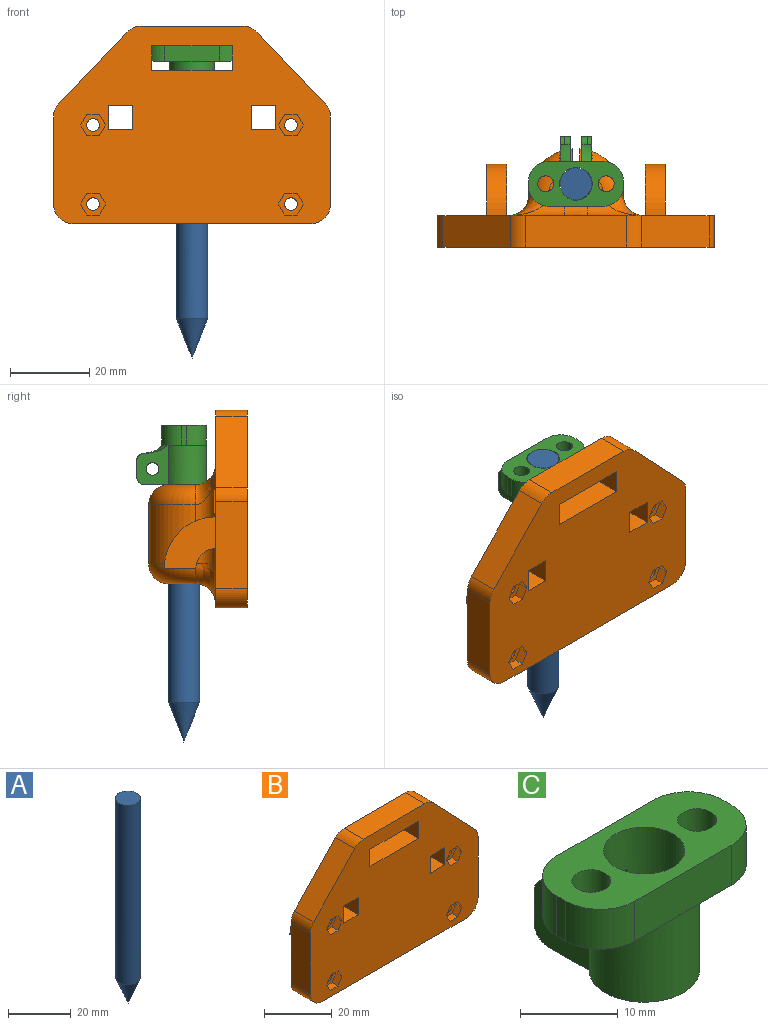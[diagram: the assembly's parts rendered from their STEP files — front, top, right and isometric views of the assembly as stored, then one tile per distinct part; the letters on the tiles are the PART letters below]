
ASSEMBLY  parts=3 mates=3
PART A: 3 faces, bbox 8x8x80 mm
  f0: cylinder r=4mm len=70mm, axis (0,0,1), area 1759.3mm2, adj f1,f2
  f1: plane 8x8mm, normal (0,0,1), area 50.3mm2, adj f0
  f2: cone r=0mm half-angle=21.8deg, axis (0,0,1), area 135.3mm2, adj f0
PART B: 189 faces, bbox 70.4x26.2x50.4 mm
  f0: plane 70x50mm, normal (0,1,0), area 1597.9mm2, adj f8,f9,f11,f12,f13,f14,f15,f16
  f1: plane 6.62x4.98mm, normal (0,0,1), area 13.5mm2, adj f6,f80,f89
  f2: plane 6.62x4.98mm, normal (0,0,-1), area 13.5mm2, adj f6,f85,f88
  f3: cylinder r=12mm len=15mm, axis (0,0,-1), area 266.9mm2, adj f69,f77,f78,f89,f90
  f4: plane 6.62x4.98mm, normal (0,0,1), area 13.5mm2, adj f6,f84,f92
  f5: plane 6.62x4.98mm, normal (0,0,-1), area 13.5mm2, adj f6,f77,f81
  f6: cylinder r=4.15mm len=25mm, axis (0,0,1), area 601.4mm2, adj f1,f2,f4,f5,f69,f70,f77,f82
  f7: plane 8x5mm, normal (0,0,-1), area 40mm2, adj f8,f9,f61,f64
  f8: cylinder r=5mm len=5mm, axis (-1,0,0), area 39.3mm2, adj f0,f7,f61,f64
  f9: cylinder r=13mm len=13mm, axis (-1,0,0), area 102.1mm2, adj f0,f7,f61,f64
  f10: plane 70x50mm, normal (0,-1,0), area 2758.9mm2, adj f15,f16,f17,f18,f19,f20,f21,f22
  f11: cylinder r=1.6mm len=5.5mm, axis (0,-1,0), area 55.3mm2, adj f0,f51
  f12: cylinder r=1.6mm len=5.5mm, axis (0,-1,0), area 55.3mm2, adj f0,f44
  f13: cylinder r=1.6mm len=5.5mm, axis (0,-1,0), area 55.3mm2, adj f0,f37
  f14: cylinder r=1.6mm len=5.5mm, axis (0,-1,0), area 55.3mm2, adj f0,f30
  f15: plane 22x8mm, normal (-1,0,0), area 176mm2, adj f0,f10,f74,f75
  f16: plane 60x8mm, normal (0,0,-1), area 480mm2, adj f0,f10,f75,f76
  f17: plane 22x8mm, normal (1,0,0), area 176mm2, adj f0,f10,f71,f76
  f18: plane 8.42x6.2mm, normal (0,0,-1), area 49.9mm2, adj f0,f10,f19,f21,f78
  f19: plane 8x6.2mm, normal (1,0,0), area 49.6mm2, adj f0,f10,f18,f20
  f20: plane 8.42x6.2mm, normal (0,0,1), area 49.9mm2, adj f0,f10,f19,f21,f78
  f21: plane 8.42x6.2mm, normal (-1,0,0), area 52.2mm2, adj f10,f18,f20,f78
  f22: plane 8x6.2mm, normal (-1,0,0), area 49.6mm2, adj f0,f10,f23,f25
  f23: plane 8.42x6.2mm, normal (0,0,-1), area 49.9mm2, adj f0,f10,f22,f24,f86
  f24: plane 8.42x6.2mm, normal (1,0,0), area 52.2mm2, adj f10,f23,f25,f86
  f25: plane 8.42x6.2mm, normal (0,0,1), area 49.9mm2, adj f0,f10,f22,f24,f86
  f26: plane 20.4x8mm, normal (0,0,-1), area 163.2mm2, adj f0,f10,f27,f29
  f27: plane 8x6.2mm, normal (1,0,0), area 49.6mm2, adj f0,f10,f26,f28
  f28: plane 20.4x8mm, normal (0,0,1), area 163.2mm2, adj f0,f10,f27,f29
  f29: plane 8x6.2mm, normal (-1,0,0), area 49.6mm2, adj f0,f10,f26,f28
  f30: plane 6.3x5.46mm, normal (0,-1,0), area 17.7mm2, adj f14,f31,f32,f33,f34,f35,f36
  f31: plane 3.15x2.5mm, normal (0,0,1), area 7.9mm2, adj f10,f30,f32,f36
  f32: plane 2.73x2.5mm, normal (-0.87,0,0.5), area 7.9mm2, adj f10,f30,f31,f33
  f33: plane 2.73x2.5mm, normal (-0.87,0,-0.5), area 7.9mm2, adj f10,f30,f32,f34
  f34: plane 3.15x2.5mm, normal (0,0,-1), area 7.9mm2, adj f10,f30,f33,f35
  f35: plane 2.73x2.5mm, normal (0.87,0,-0.5), area 7.9mm2, adj f10,f30,f34,f36
  f36: plane 2.73x2.5mm, normal (0.87,0,0.5), area 7.9mm2, adj f10,f30,f31,f35
  f37: plane 6.3x5.46mm, normal (0,-1,0), area 17.7mm2, adj f13,f38,f39,f40,f41,f42,f43
  f38: plane 3.15x2.5mm, normal (0,0,1), area 7.9mm2, adj f10,f37,f39,f43
  f39: plane 2.73x2.5mm, normal (-0.87,0,0.5), area 7.9mm2, adj f10,f37,f38,f40
  f40: plane 2.73x2.5mm, normal (-0.87,0,-0.5), area 7.9mm2, adj f10,f37,f39,f41
  f41: plane 3.15x2.5mm, normal (0,0,-1), area 7.9mm2, adj f10,f37,f40,f42
  f42: plane 2.73x2.5mm, normal (0.87,0,-0.5), area 7.9mm2, adj f10,f37,f41,f43
  f43: plane 2.73x2.5mm, normal (0.87,0,0.5), area 7.9mm2, adj f10,f37,f38,f42
  f44: plane 6.4x5.54mm, normal (0,-1,0), area 18.6mm2, adj f12,f45,f46,f47,f48,f49,f50
  f45: plane 3.2x2.5mm, normal (0,0,1), area 8mm2, adj f10,f44,f46,f50
  f46: plane 2.77x2.5mm, normal (-0.87,0,0.5), area 8mm2, adj f10,f44,f45,f47
  f47: plane 2.77x2.5mm, normal (-0.87,0,-0.5), area 8mm2, adj f10,f44,f46,f48
  f48: plane 3.2x2.5mm, normal (0,0,-1), area 8mm2, adj f10,f44,f47,f49
  f49: plane 2.77x2.5mm, normal (0.87,0,-0.5), area 8mm2, adj f10,f44,f48,f50
  f50: plane 2.77x2.5mm, normal (0.87,0,0.5), area 8mm2, adj f10,f44,f45,f49
  f51: plane 6.4x5.54mm, normal (0,-1,0), area 18.6mm2, adj f11,f52,f53,f54,f55,f56,f57
  f52: plane 2.77x2.5mm, normal (-0.87,0,0.5), area 8mm2, adj f10,f51,f53,f57
  f53: plane 2.77x2.5mm, normal (-0.87,0,-0.5), area 8mm2, adj f10,f51,f52,f54
  f54: plane 3.2x2.5mm, normal (0,0,-1), area 8mm2, adj f10,f51,f53,f55
  f55: plane 2.77x2.5mm, normal (0.87,0,-0.5), area 8mm2, adj f10,f51,f54,f56
  f56: plane 2.77x2.5mm, normal (0.87,0,0.5), area 8mm2, adj f10,f51,f55,f57
  f57: plane 3.2x2.5mm, normal (0,0,1), area 8mm2, adj f10,f51,f52,f56
  f58: cylinder r=5mm len=5mm, axis (-1,0,0), area 39.3mm2, adj f0,f59,f62,f63
  f59: plane 8x5mm, normal (0,0,-1), area 40mm2, adj f58,f60,f62,f63
  f60: cylinder r=13mm len=13mm, axis (-1,0,0), area 102.1mm2, adj f0,f59,f62,f63
  f61: plane 13x13mm, normal (1,0,0), area 113.1mm2, adj f0,f7,f8,f9
  f62: plane 13x13mm, normal (-1,0,0), area 113.1mm2, adj f0,f58,f59,f60
  f63: plane 13x13mm, normal (1,0,0), area 113.1mm2, adj f0,f58,f59,f60
  f64: plane 13x13mm, normal (-1,0,0), area 113.1mm2, adj f0,f7,f8,f9
  f65: cylinder r=12mm len=15mm, axis (0,0,-1), area 266.9mm2, adj f70,f86,f88,f92,f93
  f66: plane 18x17.15mm, normal (0.72,0,0.69), area 198.9mm2, adj f0,f10,f71,f72
  f67: plane 25.7x8mm, normal (0,0,1), area 205.6mm2, adj f0,f10,f72,f73
  f68: plane 18x17.15mm, normal (-0.72,0,0.69), area 198.9mm2, adj f0,f10,f73,f74
  f69: plane 25.36x5.21mm, normal (1,0,0), area 110.5mm2, adj f3,f6,f77,f89
  f70: plane 25.36x5.21mm, normal (-1,0,0), area 110.5mm2, adj f6,f65,f88,f92
  f71: cylinder r=5mm len=8mm, axis (0,-1,0), area 30.4mm2, adj f0,f10,f17,f66
  f72: cylinder r=5mm len=8mm, axis (0,1,0), area 32.4mm2, adj f0,f10,f66,f67
  f73: cylinder r=5mm len=8mm, axis (0,-1,0), area 32.4mm2, adj f0,f10,f67,f68
  f74: cylinder r=5mm len=8mm, axis (0,-1,0), area 30.4mm2, adj f0,f10,f15,f68
  f75: cylinder r=5mm len=8mm, axis (0,1,0), area 62.8mm2, adj f0,f10,f15,f16
  f76: cylinder r=5mm len=8mm, axis (0,-1,0), area 62.8mm2, adj f0,f10,f16,f17
  f77: torus R=7mm, axis (0,0,1), area 116.1mm2, adj f3,f5,f6,f69,f79
  f78: cylinder r=5mm len=25mm, axis (0,0,-1), area 133.2mm2, adj f0,f3,f18,f20,f21,f79,f91
  f79: bspline ~11.44x10.58mm, area 84mm2, adj f0,f77,f78,f81
  f80: cylinder r=5mm len=14.13mm, axis (-1,0,0), area 61mm2, adj f0,f1,f82,f90,f91
  f81: cylinder r=5mm len=5mm, axis (1,0,0), area 32.5mm2, adj f0,f5,f79,f83
  f82: bspline ~5.74x5mm, area 40.5mm2, adj f0,f6,f80,f84
  f83: bspline ~5.74x5mm, area 40.5mm2, adj f0,f6,f81,f85
  f84: cylinder r=5mm len=14.13mm, axis (-1,0,0), area 61mm2, adj f0,f4,f82,f93,f94
  f85: cylinder r=5mm len=5mm, axis (1,0,0), area 32.5mm2, adj f0,f2,f83,f87
  f86: cylinder r=5mm len=25mm, axis (0,0,-1), area 133.2mm2, adj f0,f23,f24,f25,f65,f87,f94
  f87: bspline ~11.72x11.68mm, area 84mm2, adj f0,f85,f86,f88
  f88: torus R=7mm, axis (0,0,1), area 116.1mm2, adj f2,f6,f65,f70,f87
  f89: torus R=7mm, axis (0,0,1), area 115.9mm2, adj f1,f3,f6,f69,f90
  f90: bspline ~5x5mm, area 0.4mm2, adj f3,f80,f89,f91
  f91: bspline ~10x10mm, area 47.1mm2, adj f78,f80,f90
  f92: torus R=7mm, axis (0,0,1), area 115.9mm2, adj f4,f6,f65,f70,f93
  f93: bspline ~5x5mm, area 0.4mm2, adj f65,f84,f92,f94
  f94: bspline ~10x10mm, area 47.1mm2, adj f84,f86,f93
  f95: plane 0.55x0.5mm, normal (1,0,0), area 0.3mm2, adj f0,f96,f103,f104
  f96: plane 4.96x0.5mm, normal (0,0,-1), area 2.5mm2, adj f0,f95,f97,f104
  f97: plane 0.5x0.47mm, normal (-1,0,0), area 0.2mm2, adj f0,f96,f98,f104
  f98: plane 1.31x1.01mm, normal (-0.79,0,0.61), area 0.8mm2, adj f0,f97,f99,f104
  f99: plane 0.5x0.39mm, normal (0.61,0,0.79), area 0.2mm2, adj f0,f98,f100,f104
  f100: extruded ~0.81x0.66mm, area 0.5mm2, adj f0,f99,f101,f104
  f101: extruded ~0.5x0.16mm, area 0.1mm2, adj f0,f100,f102,f104
  f102: extruded ~0.83x0.5mm, area 0.4mm2, adj f0,f101,f103,f104
  f103: plane 3.53x0.5mm, normal (0,0,1), area 1.8mm2, adj f0,f95,f102,f104
  f104: plane 4.96x1.79mm, normal (0,1,0), area 3.4mm2, adj f95,f96,f97,f98,f99,f100,f101,f102
  f105: extruded ~0.5x0.34mm, area 0.2mm2, adj f0,f106,f112,f113
  f106: extruded ~0.5x0.35mm, area 0.2mm2, adj f0,f105,f107,f113
  f107: extruded ~0.5x0.29mm, area 0.2mm2, adj f0,f106,f108,f113
  f108: extruded ~0.5x0.31mm, area 0.2mm2, adj f0,f107,f109,f113
  f109: extruded ~0.5x0.34mm, area 0.2mm2, adj f0,f108,f110,f113
  f110: extruded ~0.5x0.34mm, area 0.2mm2, adj f0,f109,f111,f113
  f111: extruded ~0.5x0.31mm, area 0.2mm2, adj f0,f110,f112,f113
  f112: extruded ~0.5x0.3mm, area 0.2mm2, adj f0,f105,f111,f113
  f113: plane 0.92x0.82mm, normal (0,1,0), area 0.6mm2, adj f105,f106,f107,f108,f109,f110,f111,f112
  f114: plane 3.26x0.5mm, normal (1,0,0), area 1.6mm2, adj f0,f115,f133,f134
  f115: plane 0.52x0.5mm, normal (0,0,-1), area 0.3mm2, adj f0,f114,f116,f134
  f116: plane 2.55x0.5mm, normal (-1,0,0), area 1.3mm2, adj f0,f115,f117,f134
  f117: plane 0.5x0.03mm, normal (0,0,-1), area 0mm2, adj f0,f116,f118,f134
  f118: plane 1.09x1.06mm, normal (0.71,0,-0.7), area 0.8mm2, adj f0,f117,f119,f134
  f119: extruded ~1.17x0.99mm, area 0.8mm2, adj f0,f118,f120,f134
  f120: extruded ~0.93x0.5mm, area 0.5mm2, adj f0,f119,f121,f134
  f121: extruded ~0.96x0.5mm, area 0.5mm2, adj f0,f120,f122,f134
  f122: extruded ~1.1x0.5mm, area 0.6mm2, adj f0,f121,f123,f134
  f123: extruded ~1.49x0.57mm, area 0.8mm2, adj f0,f122,f124,f134
  f124: plane 0.5x0.38mm, normal (0.61,0,0.79), area 0.2mm2, adj f0,f123,f125,f134
  f125: extruded ~0.62x0.5mm, area 0.4mm2, adj f0,f124,f126,f134
  f126: extruded ~0.59x0.5mm, area 0.3mm2, adj f0,f125,f127,f134
  f127: extruded ~0.67x0.5mm, area 0.4mm2, adj f0,f126,f128,f134
  f128: extruded ~0.63x0.5mm, area 0.3mm2, adj f0,f127,f129,f134
  f129: extruded ~0.53x0.5mm, area 0.3mm2, adj f0,f128,f130,f134
  f130: extruded ~0.5x0.5mm, area 0.3mm2, adj f0,f129,f131,f134
  f131: extruded ~0.86x0.79mm, area 0.6mm2, adj f0,f130,f132,f134
  f132: plane 1.31x1.31mm, normal (-0.71,0,0.71), area 0.9mm2, adj f0,f131,f133,f134
  f133: plane 0.5x0.49mm, normal (0,0,1), area 0.2mm2, adj f0,f114,f132,f134
  f134: plane 5.03x3.26mm, normal (0,1,0), area 5.4mm2, adj f114,f115,f116,f117,f118,f119,f120,f121
  f135: extruded ~0.5x0.5mm, area 0.3mm2, adj f0,f136,f144,f145
  f136: extruded ~0.94x0.5mm, area 0.5mm2, adj f0,f135,f137,f145
  f137: extruded ~1x0.5mm, area 0.5mm2, adj f0,f136,f138,f145
  f138: plane 4.91x0.5mm, normal (1,0,0), area 2.5mm2, adj f0,f137,f139,f145
  f139: plane 0.58x0.5mm, normal (0,0,-1), area 0.3mm2, adj f0,f138,f140,f145
  f140: plane 4.96x0.5mm, normal (-1,0,0), area 2.5mm2, adj f0,f139,f141,f145
  f141: extruded ~0.59x0.5mm, area 0.3mm2, adj f0,f140,f142,f145
  f142: extruded ~0.51x0.5mm, area 0.3mm2, adj f0,f141,f143,f145
  f143: extruded ~0.5x0.5mm, area 0.3mm2, adj f0,f142,f144,f145
  f144: plane 0.5x0.49mm, normal (-1,0,0), area 0.2mm2, adj f0,f135,f143,f145
  f145: plane 6.26x1.76mm, normal (0,1,0), area 4mm2, adj f135,f136,f137,f138,f139,f140,f141,f142
  f146: extruded ~0.5x0.28mm, area 0.2mm2, adj f0,f147,f153,f154
  f147: extruded ~0.5x0.28mm, area 0.2mm2, adj f0,f146,f148,f154
  f148: extruded ~0.5x0.24mm, area 0.1mm2, adj f0,f147,f149,f154
  f149: extruded ~0.5x0.23mm, area 0.1mm2, adj f0,f148,f150,f154
  f150: extruded ~0.5x0.28mm, area 0.2mm2, adj f0,f149,f151,f154
  f151: extruded ~0.5x0.28mm, area 0.2mm2, adj f0,f150,f152,f154
  f152: extruded ~0.5x0.23mm, area 0.1mm2, adj f0,f151,f153,f154
  f153: extruded ~0.5x0.24mm, area 0.1mm2, adj f0,f146,f152,f154
  f154: plane 0.75x0.67mm, normal (0,1,0), area 0.4mm2, adj f146,f147,f148,f149,f150,f151,f152,f153
  f155: plane 0.56x0.5mm, normal (0,0,1), area 0.3mm2, adj f0,f156,f158,f159
  f156: plane 3.72x0.5mm, normal (1,0,0), area 1.9mm2, adj f0,f155,f157,f159
  f157: plane 0.56x0.5mm, normal (0,0,-1), area 0.3mm2, adj f0,f156,f158,f159
  f158: plane 3.72x0.5mm, normal (-1,0,0), area 1.9mm2, adj f0,f155,f157,f159
  f159: plane 3.72x0.56mm, normal (0,1,0), area 2.1mm2, adj f155,f156,f157,f158
  f160: plane 4.39x1.68mm, normal (-0.93,0,0.36), area 2.4mm2, adj f0,f161,f177,f178
  f161: plane 0.5x0.46mm, normal (0,0,1), area 0.2mm2, adj f0,f160,f162,f178
  f162: plane 4.39x1.7mm, normal (0.93,0,0.36), area 2.4mm2, adj f0,f161,f163,f178
  f163: plane 0.5x0.03mm, normal (0,0,1), area 0mm2, adj f0,f162,f164,f178
  f164: extruded ~1.19x0.5mm, area 0.6mm2, adj f0,f163,f165,f178
  f165: plane 3.19x0.5mm, normal (-1,0,0), area 1.6mm2, adj f0,f164,f166,f178
  f166: plane 0.58x0.5mm, normal (0,0,1), area 0.3mm2, adj f0,f165,f167,f178
  f167: plane 4.96x0.5mm, normal (1,0,0), area 2.5mm2, adj f0,f166,f168,f178
  f168: plane 0.86x0.5mm, normal (0,0,-1), area 0.4mm2, adj f0,f167,f169,f178
  f169: plane 4.09x1.58mm, normal (-0.93,0,-0.36), area 2.2mm2, adj f0,f168,f170,f178
  f170: plane 0.5x0.03mm, normal (0,0,-1), area 0mm2, adj f0,f169,f171,f178
  f171: plane 4.09x1.57mm, normal (0.93,0,-0.36), area 2.2mm2, adj f0,f170,f172,f178
  f172: plane 0.87x0.5mm, normal (0,0,-1), area 0.4mm2, adj f0,f171,f173,f178
  f173: plane 4.96x0.5mm, normal (-1,0,0), area 2.5mm2, adj f0,f172,f174,f178
  f174: plane 0.53x0.5mm, normal (0,0,1), area 0.3mm2, adj f0,f173,f175,f178
  f175: plane 3.15x0.5mm, normal (1,0,0), area 1.6mm2, adj f0,f174,f176,f178
  f176: extruded ~1.24x0.5mm, area 0.6mm2, adj f0,f175,f177,f178
  f177: plane 0.5x0.03mm, normal (0,0,1), area 0mm2, adj f0,f160,f176,f178
  f178: plane 4.96x4.91mm, normal (0,1,0), area 10.5mm2, adj f160,f161,f162,f163,f164,f165,f166,f167
  f179: plane 0.62x0.5mm, normal (-1,0,0), area 0.3mm2, adj f0,f180,f187,f188
  f180: plane 3.19x1.13mm, normal (-0.33,0,0.94), area 1.7mm2, adj f0,f179,f181,f188
  f181: extruded ~1.1x0.5mm, area 0.6mm2, adj f0,f180,f182,f188
  f182: extruded ~1.08x0.5mm, area 0.6mm2, adj f0,f181,f183,f188
  f183: plane 3.21x1.14mm, normal (-0.33,0,-0.94), area 1.7mm2, adj f0,f182,f184,f188
  f184: plane 0.61x0.5mm, normal (-1,0,0), area 0.3mm2, adj f0,f183,f185,f188
  f185: plane 4.96x1.78mm, normal (0.34,0,0.94), area 2.6mm2, adj f0,f184,f186,f188
  f186: plane 0.57x0.5mm, normal (1,0,0), area 0.3mm2, adj f0,f185,f187,f188
  f187: plane 4.96x1.79mm, normal (0.34,0,-0.94), area 2.6mm2, adj f0,f179,f186,f188
  f188: plane 4.96x4.13mm, normal (0,1,0), area 5.7mm2, adj f179,f180,f181,f182,f183,f184,f185,f186
PART C: 33 faces, bbox 24.8x22.4x15.8 mm
  f0: plane 24x11.3mm, normal (0,0,-1), area 128.9mm2, adj f1,f2,f3,f4,f5,f7,f9,f10
  f1: cylinder r=5.65mm len=11.3mm, axis (0,0,1), area 266.1mm2, adj f0,f8,f11,f14
  f2: plane 14x5mm, normal (0,1,0), area 70mm2, adj f0,f6,f21,f24
  f3: plane 5x1.3mm, normal (-1,0,0), area 6.5mm2, adj f0,f6,f21,f22
  f4: plane 14x5mm, normal (0,-1,0), area 70mm2, adj f0,f6,f22,f23
  f5: plane 5x1.3mm, normal (1,0,0), area 6.5mm2, adj f0,f6,f23,f24
  f6: plane 24x11.3mm, normal (0,0,1), area 157.9mm2, adj f2,f3,f4,f5,f7,f19,f20,f21
  f7: cylinder r=4.15mm len=15mm, axis (0,0,1), area 360.4mm2, adj f0,f6,f8,f9,f10
  f8: plane 15.6x11.3mm, normal (0,0,-1), area 67mm2, adj f1,f7,f9,f10,f11,f14,f27,f30
  f9: plane 10.19x8.27mm, normal (-1,0,0), area 61mm2, adj f0,f7,f8,f13,f18,f26,f30,f32
  f10: plane 10.2x8.28mm, normal (1,0,0), area 61mm2, adj f0,f7,f8,f16,f17,f25,f27,f29
  f11: plane 10.75x8.71mm, normal (1,0,0), area 57.6mm2, adj f1,f8,f12,f13,f18,f26,f30,f31
  f12: plane 1.19x0.41mm, normal (0,0,1), area 0.2mm2, adj f11,f26,f31
  f13: plane 4x2.5mm, normal (0,1,0), area 10mm2, adj f9,f11,f30,f31,f32
  f14: plane 10.75x8.71mm, normal (-1,0,0), area 57.6mm2, adj f1,f8,f15,f16,f17,f25,f27,f28
  f15: plane 1.19x0.41mm, normal (0,0,1), area 0.2mm2, adj f14,f25,f28
  f16: plane 4x2.5mm, normal (0,1,0), area 10mm2, adj f10,f14,f27,f28,f29
  f17: cylinder r=1.6mm len=3.2mm, axis (-1,0,0), area 25.1mm2, adj f10,f14
  f18: cylinder r=1.6mm len=3.2mm, axis (-1,0,0), area 25.1mm2, adj f9,f11
  f19: cylinder r=2mm len=5mm, axis (0,0,-1), area 62.8mm2, adj f0,f6
  f20: cylinder r=2mm len=5mm, axis (0,0,-1), area 125.7mm2, adj f0,f6
  f21: cylinder r=5mm len=5mm, axis (0,0,1), area 39.3mm2, adj f0,f2,f3,f6
  f22: cylinder r=5mm len=5mm, axis (0,0,-1), area 39.3mm2, adj f0,f3,f4,f6
  f23: cylinder r=5mm len=5mm, axis (0,0,1), area 39.3mm2, adj f0,f4,f5,f6
  f24: cylinder r=5mm len=5mm, axis (0,0,-1), area 39.3mm2, adj f0,f2,f5,f6
  f25: torus R=10.34mm, axis (0,0,1), area 15.2mm2, adj f0,f10,f14,f15,f29
  f26: torus R=10.34mm, axis (0,0,-1), area 15.2mm2, adj f0,f9,f11,f12,f32
  f27: cylinder r=2mm len=2.5mm, axis (1,0,0), area 7.9mm2, adj f8,f10,f14,f16
  f28: cylinder r=2mm len=2mm, axis (1,0,0), area 3.7mm2, adj f14,f15,f16,f29
  f29: bspline ~4.52x2.17mm, area 4.1mm2, adj f10,f16,f25,f28
  f30: cylinder r=2mm len=2.5mm, axis (-1,0,0), area 7.9mm2, adj f8,f9,f11,f13
  f31: cylinder r=2mm len=2mm, axis (1,0,0), area 3.7mm2, adj f11,f12,f13,f32
  f32: bspline ~6.45x2.46mm, area 4.1mm2, adj f9,f13,f26,f31
PLACE A t=(-33.75,-19.59,85.29)mm
PLACE B t=(-33.75,-27.59,89.19)mm
PLACE C t=(-33.75,-25.24,55.29)mm
MATE fastened C.f1 <-> A.f0  axis (0,0,1) through (-33.75,-19.59,85.29)mm
MATE slider B.f6 <-> A.f0  axis (0,0,1) through (-33.75,-19.59,45.29)mm
MATE planar C.f8 <-> B.f4  axis (0,0,-1) through (-33.75,-17.11,70.29)mm
